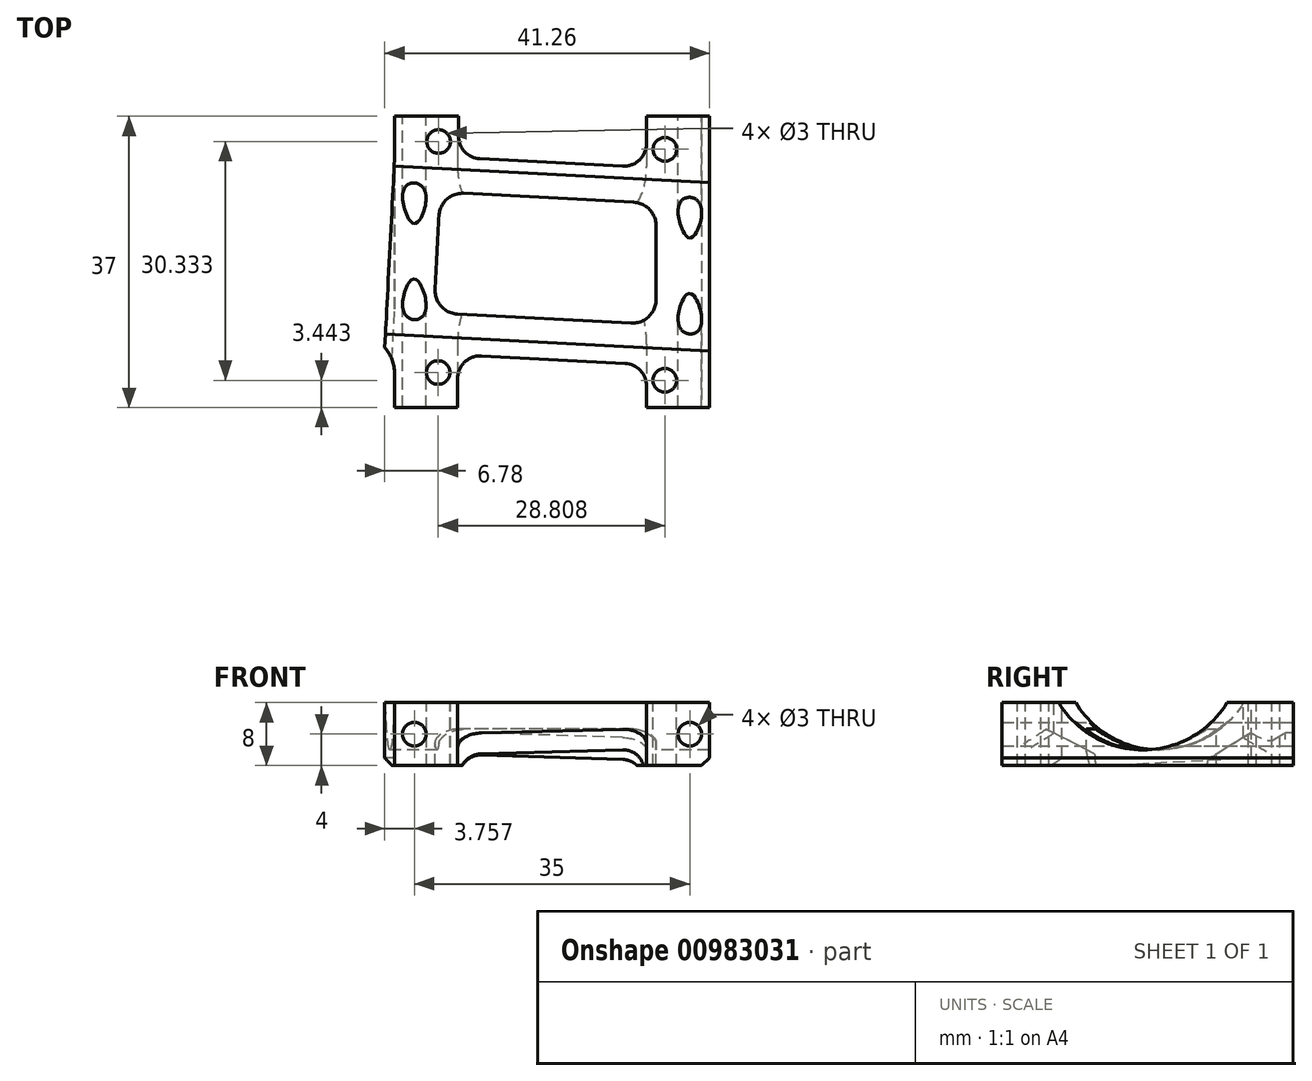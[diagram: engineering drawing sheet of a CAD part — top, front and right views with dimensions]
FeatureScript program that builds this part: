
annotation { "Feature Type Name" : "Feature", "Feature Type Description" : "" }
export const myFeature = defineFeature(function(context is Context, id is Id, definition is map)
    precondition{}
    {
        {
            var Q0;
            Q0=qCreatedBy(makeId("Top.planeOp"),FACE);
            var sketch = newSketch(context, id + "F0", { "sketchPlane" : qUnion([Q0])});
            skLineSegment(sketch, "E0.bottom", {"start": v(-25.77, 33.29) * mm, "end": v(14.23, 33.29) * mm});
            skLineSegment(sketch, "E0.top", {"start": v(-25.77, -1.71) * mm, "end": v(14.23, -1.71) * mm});
            skLineSegment(sketch, "E0.left", {"start": v(-25.77, 33.29) * mm, "end": v(-25.77, -1.71) * mm});
            skLineSegment(sketch, "E0.right", {"start": v(14.23, 33.29) * mm, "end": v(14.23, -1.71) * mm});
            skSolve(sketch);
        }
        {
            var Q0;
            Q0 = qSketchRegion(id + "F0", true);
            extrude(context, id + "F1", {"entities" : qUnion([Q0]), "depth" : 8 * mm, "offsetDistance" : 25 * mm});
        }
        {
            var Q0;
            Q0=makeQuery(id+"F1.opExtrude","CAP_FACE",FACE,{"disambiguationData":[OSD([sQuery(id+"F0.wireOp",EDGE,"E0.bottom"),sQuery(id+"F0.wireOp",EDGE,"E0.top"),sQuery(id+"F0.wireOp",EDGE,"E0.left"),sQuery(id+"F0.wireOp",EDGE,"E0.right")])],"isStart":false});
            var sketch = newSketch(context, id + "F2", { "sketchPlane" : qUnion([Q0])});
            skLineSegment(sketch, "E1", {"start": v(-25.77, 28.93) * mm, "end": v(-27.03, 4.89) * mm});
            skLineSegment(sketch, "E2", {"start": v(-27.03, 4.89) * mm, "end": v(-25.77, 4.82) * mm});
            skLineSegment(sketch, "E3", {"start": v(-25.77, 4.82) * mm, "end": v(-23.4, 26.1) * mm});
            skLineSegment(sketch, "E4", {"start": v(-23.4, 26.1) * mm, "end": v(-25.77, 28.93) * mm});
            skSolve(sketch);
        }
        {
            var Q0;
            Q0 = qSketchRegion(id + "F2", true);
            extrude(context, id + "F3", {"entities" : qUnion([Q0]), "operationType" : NewBodyOperationType.ADD, "oppositeDirection" : true, "depth" : 8 * mm, "offsetDistance" : 25 * mm});
        }
        {
            var Q0;
            Q0=makeQuery(id+"F3.opExtrude","SWEPT_FACE",FACE,{"disambiguationData":[OSD([sQuery(id+"F2.wireOp",EDGE,"E1")])]});
            var sketch = newSketch(context, id + "F4", { "sketchPlane" : qUnion([Q0])});
            skCircle(sketch, "E5", {"center": v(-15.9, 14.5) * mm, "radius": 12.5 * mm});
            skSolve(sketch);
        }
        {
            var Q0;
            Q0 = qSketchRegion(id + "F4", true);
            extrude(context, id + "F5", {"entities" : qUnion([Q0]), "operationType" : NewBodyOperationType.REMOVE, "oppositeDirection" : true, "depth" : 64.1 * mm, "offsetDistance" : 25 * mm});
        }
        {
            var Q0;
            {var subQ1=sQuery(id+"F0.wireOp",EDGE,"E0.left");var subQ2=sQuery(id+"F0.wireOp",EDGE,"E0.right");var subQ3=sQuery(id+"F0.wireOp",EDGE,"E0.bottom");Q0=makeQuery(id+"F5.boolean.opBoolean","SPLIT",FACE,{"disambiguationData":[TD([makeQuery(id+"F1.opExtrude","SWEPT_FACE",FACE,{"disambiguationData":[OSD([subQ3])]})])],"derivedFrom":makeQuery(id+"F3.boolean.opBoolean","MERGE",FACE,{"derivedFrom":[makeQuery(id+"F1.opExtrude","CAP_FACE",FACE,{"disambiguationData":[OSD([subQ3,sQuery(id+"F0.wireOp",EDGE,"E0.top"),subQ1,subQ2])],"isStart":false}),makeQuery(id+"F3.opExtrude","CAP_FACE",FACE,{"disambiguationData":[OSD([sQuery(id+"F2.wireOp",EDGE,"E1"),sQuery(id+"F2.wireOp",EDGE,"E2"),sQuery(id+"F2.wireOp",EDGE,"E3"),sQuery(id+"F2.wireOp",EDGE,"E4")])],"isStart":true})]})});}
            var sketch = newSketch(context, id + "F6", { "sketchPlane" : qUnion([Q0])});
            skLineSegment(sketch, "E6", {"start": v(-14.93, 28.9) * mm, "end": v(3.18, 27.94) * mm});
            skLineSegment(sketch, "E7.0", {"start": v(-14.72, 3.85) * mm, "end": v(3.48, 2.9) * mm});
            skLineSegment(sketch, "E8.0", {"start": v(6.23, 0) * mm, "end": v(6.23, -1.71) * mm});
            skLineSegment(sketch, "E9.0", {"start": v(-17.77, 0.95) * mm, "end": v(-17.77, -1.71) * mm});
            skLineSegment(sketch, "E10.0", {"start": v(6.23, 33.29) * mm, "end": v(6.23, 30.84) * mm});
            skCircle(sketch, "E11", {"center": v(-20.25, 1.73) * mm, "radius": 1.5 * mm});
            skCircle(sketch, "E12", {"center": v(8.56, 30.09) * mm, "radius": 1.5 * mm});
            skCircle(sketch, "E13", {"center": v(-20.2, 31.07) * mm, "radius": 1.5 * mm});
            skLineSegment(sketch, "E14", {"start": v(-17.68, 31.79) * mm, "end": v(-17.68, 33.29) * mm});
            skPoint(sketch, "E15.visualSharp", {"position": v(-17.68, 29.04) * mm});
            skArc(sketch, "E15.filletArc", {"start": v(-17.68, 31.79) * mm, "mid": v(-16.88, 29.8) * mm, "end": v(-14.93, 28.9) * mm});
            skPoint(sketch, "E16.visualSharp", {"position": v(6.23, 27.78) * mm});
            skArc(sketch, "E16.filletArc", {"start": v(3.18, 27.94) * mm, "mid": v(5.32, 28.74) * mm, "end": v(6.23, 30.84) * mm});
            skPoint(sketch, "E17.visualSharp", {"position": v(6.23, 2.75) * mm});
            skArc(sketch, "E17.filletArc", {"start": v(6.23, 0) * mm, "mid": v(5.43, 2) * mm, "end": v(3.48, 2.9) * mm});
            skPoint(sketch, "E18.visualSharp", {"position": v(-17.77, 4) * mm});
            skArc(sketch, "E18.filletArc", {"start": v(-14.72, 3.85) * mm, "mid": v(-16.87, 3.05) * mm, "end": v(-17.77, 0.95) * mm});
            skLineSegment(sketch, "E19", {"start": v(-17.77, -1.71) * mm, "end": v(-10.84, -6.86) * mm});
            skLineSegment(sketch, "E20", {"start": v(-10.84, -6.86) * mm, "end": v(6.23, -1.71) * mm});
            skLineSegment(sketch, "E21", {"start": v(-17.68, 33.29) * mm, "end": v(-3.16, 37.2) * mm});
            skLineSegment(sketch, "E22", {"start": v(-3.16, 37.2) * mm, "end": v(6.23, 33.29) * mm});
            skCircle(sketch, "E23", {"center": v(8.55, 0.73) * mm, "radius": 1.5 * mm});
            skSolve(sketch);
        }
        {
            var Q0;
            Q0 = qSketchRegion(id + "F6", true);
            extrude(context, id + "F7", {"entities" : qUnion([Q0]), "operationType" : NewBodyOperationType.REMOVE, "oppositeDirection" : true, "depth" : 25 * mm, "offsetDistance" : 25 * mm});
        }
        {
            var Q0;
            {var subQ5=sQuery(id+"F0.wireOp",EDGE,"E0.left");var subQ7=sQuery(id+"F0.wireOp",EDGE,"E0.bottom");Q0=makeQuery(id+"F7.boolean.opBoolean","SPLIT",FACE,{"disambiguationData":[TD([makeQuery(id+"F1.opExtrude","SWEPT_FACE",FACE,{"disambiguationData":[OSD([subQ5])]})])],"derivedFrom":makeQuery(id+"F1.opExtrude","SWEPT_FACE",FACE,{"disambiguationData":[OSD([subQ7])]})});}
            var sketch = newSketch(context, id + "F8", { "sketchPlane" : qUnion([Q0])});
            skCircle(sketch, "E24", {"center": v(-11.73, 4) * mm, "radius": 1.5 * mm});
            skCircle(sketch, "E25", {"center": v(23.27, 4) * mm, "radius": 1.5 * mm});
            skSolve(sketch);
        }
        {
            var Q0;
            Q0 = qSketchRegion(id + "F8", true);
            extrude(context, id + "F9", {"entities" : qUnion([Q0]), "operationType" : NewBodyOperationType.REMOVE, "oppositeDirection" : true, "depth" : 46.6 * mm, "offsetDistance" : 25 * mm});
        }
        {
            var Q0;
            Q0=makeQuery(id+"F3.opExtrude","SWEPT_EDGE",EDGE,{"disambiguationData":[OSD([sQuery(id+"F0.wireOp",EDGE,"E0.left"),sQuery(id+"F2.wireOp",EDGE,"E2"),sQuery(id+"F2.wireOp",EDGE,"E3")])]});
            fillet(context, id + "F10", {"entities" : qUnion([Q0]), "radius" : 5 * mm, "tangentPropagation" : true, "allowEdgeOverflow" : false});
        }
        {
            var Q0;
            Q0=makeQuery(id+"F7.boolean.opBoolean","COPY",FACE,{"derivedFrom":makeQuery(id+"F7.opExtrude","SWEPT_FACE",FACE,{"disambiguationData":[OSD([sQuery(id+"F6.wireOp",EDGE,"E8.0")])]})});
            var sketch = newSketch(context, id + "F11", { "sketchPlane" : qUnion([Q0])});
            skLineSegment(sketch, "E26", {"start": v(-37.97, 9.77) * mm, "end": v(-21.04, -0.7) * mm});
            skLineSegment(sketch, "E27", {"start": v(-13.35, -0.7) * mm, "end": v(0, 6.1) * mm});
            skLineSegment(sketch, "E28", {"start": v(-37.97, 9.77) * mm, "end": v(-37.97, -11.82) * mm});
            skLineSegment(sketch, "E29", {"start": v(-37.97, -11.82) * mm, "end": v(-21.04, -0.7) * mm});
            skLineSegment(sketch, "E30", {"start": v(-13.35, -0.7) * mm, "end": v(-2.57, -3.45) * mm});
            skLineSegment(sketch, "E31", {"start": v(0, 6.1) * mm, "end": v(4.72, 8.5) * mm});
            skLineSegment(sketch, "E32", {"start": v(4.72, 8.5) * mm, "end": v(6.07, -10.58) * mm});
            skLineSegment(sketch, "E33", {"start": v(6.07, -10.58) * mm, "end": v(-2.57, -3.45) * mm});
            skSolve(sketch);
        }
        {
            var Q0;
            Q0 = qSketchRegion(id + "F11", true);
            var Q1;
            Q1=makeQuery(id+"F7.boolean.opBoolean","COPY",FACE,{"derivedFrom":makeQuery(id+"F7.opExtrude","SWEPT_FACE",FACE,{"disambiguationData":[OSD([sQuery(id+"F6.wireOp",EDGE,"E9.0")])]})});
            extrude(context, id + "F12", {"entities" : qUnion([Q0]), "operationType" : NewBodyOperationType.REMOVE, "endBound" : BoundingType.UP_TO_SURFACE, "depth" : 25 * mm, "endBoundEntityFace" : qUnion([Q1]), "offsetDistance" : 25 * mm});
        }
        {
            var Q0;
            Q0=makeQuery(id+"F12.boolean.opBoolean","COPY",EDGE,{"derivedFrom":makeQuery(id+"F12.opExtrude","CAP_EDGE",EDGE,{"disambiguationData":[OSD([sQuery(id+"F11.wireOp",EDGE,"E26")])],"isStart":true})});
            var Q1;
            Q1=makeQuery(id+"F12.boolean.opBoolean","COPY",EDGE,{"derivedFrom":makeQuery(id+"F12.opExtrude","CAP_EDGE",EDGE,{"disambiguationData":[OSD([sQuery(id+"F11.wireOp",EDGE,"E27")])],"isStart":false})});
            var Q2;
            Q2=makeQuery(id+"F12.boolean.opBoolean","COPY",EDGE,{"derivedFrom":makeQuery(id+"F12.opExtrude","CAP_EDGE",EDGE,{"disambiguationData":[OSD([sQuery(id+"F11.wireOp",EDGE,"E26")])],"isStart":false})});
            var Q3;
            Q3=makeQuery(id+"F12.boolean.opBoolean","COPY",EDGE,{"derivedFrom":makeQuery(id+"F12.opExtrude","CAP_EDGE",EDGE,{"disambiguationData":[OSD([sQuery(id+"F11.wireOp",EDGE,"E27")])],"isStart":true})});
            fillet(context, id + "F13", {"entities" : qUnion([Q0, Q1, Q2, Q3]), "radius" : 3 * mm, "tangentPropagation" : true, "allowEdgeOverflow" : false});
        }
        {
            var Q0;
            Q0=makeQuery(id+"F1.opExtrude","CAP_EDGE",EDGE,{"disambiguationData":[OSD([sQuery(id+"F0.wireOp",EDGE,"E0.right")])],"isStart":true});
            var Q1;
            Q1=makeQuery(id+"F3.opExtrude","CAP_EDGE",EDGE,{"disambiguationData":[OSD([sQuery(id+"F2.wireOp",EDGE,"E1")])],"isStart":false});
            chamfer(context, id + "F14", {"entities" : qUnion([Q0, Q1]), "width" : 1 * mm, "tangentPropagation" : true});
        }
        {
            var Q0;
            {var subQ4=sQuery(id+"F0.wireOp",EDGE,"E0.right");var subQ6=sQuery(id+"F0.wireOp",EDGE,"E0.top");Q0=makeQuery(id+"F7.boolean.opBoolean","SPLIT",FACE,{"disambiguationData":[TD([makeQuery(id+"F1.opExtrude","SWEPT_FACE",FACE,{"disambiguationData":[OSD([subQ4])]})])],"derivedFrom":makeQuery(id+"F1.opExtrude","SWEPT_FACE",FACE,{"disambiguationData":[OSD([subQ6])]})});}
            var Q1;
            {var subQ5=sQuery(id+"F0.wireOp",EDGE,"E0.left");var subQ6=sQuery(id+"F0.wireOp",EDGE,"E0.top");Q1=makeQuery(id+"F7.boolean.opBoolean","SPLIT",FACE,{"disambiguationData":[TD([makeQuery(id+"F1.opExtrude","SWEPT_FACE",FACE,{"disambiguationData":[OSD([subQ5])]})])],"derivedFrom":makeQuery(id+"F1.opExtrude","SWEPT_FACE",FACE,{"disambiguationData":[OSD([subQ6])]})});}
            extrude(context, id + "F15", {"entities" : qUnion([Q0, Q1]), "operationType" : NewBodyOperationType.ADD, "depth" : 1 * mm, "offsetDistance" : 25 * mm});
        }
        {
            var Q0;
            {var subQ4=sQuery(id+"F0.wireOp",EDGE,"E0.right");var subQ7=sQuery(id+"F0.wireOp",EDGE,"E0.bottom");Q0=makeQuery(id+"F7.boolean.opBoolean","SPLIT",FACE,{"disambiguationData":[TD([makeQuery(id+"F1.opExtrude","SWEPT_FACE",FACE,{"disambiguationData":[OSD([subQ4])]})])],"derivedFrom":makeQuery(id+"F1.opExtrude","SWEPT_FACE",FACE,{"disambiguationData":[OSD([subQ7])]})});}
            var Q1;
            {var subQ5=sQuery(id+"F0.wireOp",EDGE,"E0.left");var subQ7=sQuery(id+"F0.wireOp",EDGE,"E0.bottom");Q1=makeQuery(id+"F7.boolean.opBoolean","SPLIT",FACE,{"disambiguationData":[TD([makeQuery(id+"F1.opExtrude","SWEPT_FACE",FACE,{"disambiguationData":[OSD([subQ5])]})])],"derivedFrom":makeQuery(id+"F1.opExtrude","SWEPT_FACE",FACE,{"disambiguationData":[OSD([subQ7])]})});}
            extrude(context, id + "F16", {"entities" : qUnion([Q0, Q1]), "operationType" : NewBodyOperationType.ADD, "depth" : 1 * mm, "offsetDistance" : 25 * mm});
        }
        {
            var Q0;
            {var subQ0=sQuery(id+"F2.wireOp",EDGE,"E1");var subQ1=makeQuery(id+"F3.opExtrude","CAP_FACE",FACE,{"disambiguationData":[OSD([subQ0,sQuery(id+"F2.wireOp",EDGE,"E2"),sQuery(id+"F2.wireOp",EDGE,"E3"),sQuery(id+"F2.wireOp",EDGE,"E4")])],"isStart":true});var subQ2=sQuery(id+"F0.wireOp",EDGE,"E0.right");var subQ3=sQuery(id+"F0.wireOp",EDGE,"E0.left");var subQ4=sQuery(id+"F0.wireOp",EDGE,"E0.bottom");var subQ5=makeQuery(id+"F1.opExtrude","CAP_FACE",FACE,{"disambiguationData":[OSD([subQ4,sQuery(id+"F0.wireOp",EDGE,"E0.top"),subQ3,subQ2])],"isStart":false});var subQ6=makeQuery(id+"F1.opExtrude","SWEPT_FACE",FACE,{"disambiguationData":[OSD([subQ2])]});var subQ7=makeQuery(id+"F1.opExtrude","SWEPT_FACE",FACE,{"disambiguationData":[OSD([subQ4])]});var subQ8=makeQuery(id+"F1.opExtrude","CAP_EDGE",EDGE,{"disambiguationData":[OSD([subQ4])],"isStart":false});var subQ9=makeQuery(id+"F1.opExtrude","SWEPT_FACE",FACE,{"disambiguationData":[OSD([subQ3])]});Q0=makeQuery(id+"F16.boolean.opBoolean","MERGE",FACE,{"derivedFrom":[makeQuery(id+"F5.boolean.opBoolean","SPLIT",FACE,{"disambiguationData":[TD([subQ7])],"derivedFrom":makeQuery(id+"F3.boolean.opBoolean","MERGE",FACE,{"derivedFrom":[subQ5,subQ1]})}),makeQuery(id+"F16.opExtrude","SWEPT_FACE",FACE,{"disambiguationData":[OSD([subQ4]),TDD([makeQuery(id+"F7.boolean.opBoolean","SPLIT",EDGE,{"disambiguationData":[TD([subQ9])],"derivedFrom":subQ8})])]}),makeQuery(id+"F16.opExtrude","SWEPT_FACE",FACE,{"disambiguationData":[OSD([subQ4]),TDD([makeQuery(id+"F7.boolean.opBoolean","SPLIT",EDGE,{"disambiguationData":[TD([subQ6])],"derivedFrom":subQ8})])]})]});}
            var sketch = newSketch(context, id + "F17", { "sketchPlane" : qUnion([Q0])});
            skLineSegment(sketch, "E34.0", {"start": v(4.58, 23.36) * mm, "end": v(-17, 24.5) * mm});
            skLineSegment(sketch, "E34.2", {"start": v(-17.8, 9.16) * mm, "end": v(4.27, 8) * mm});
            skLineSegment(sketch, "E35.3", {"start": v(-20.15, 21.65) * mm, "end": v(-20.64, 12.31) * mm});
            skLineSegment(sketch, "E36", {"start": v(14.23, 25.86) * mm, "end": v(14.23, 2.64) * mm});
            skLineSegment(sketch, "E37.0", {"start": v(7.43, 20.37) * mm, "end": v(7.43, 11) * mm});
            skPoint(sketch, "E38.visualSharp", {"position": v(-19.99, 24.65) * mm});
            skArc(sketch, "E38.filletArc", {"start": v(-17, 24.5) * mm, "mid": v(-19.16, 23.73) * mm, "end": v(-20.15, 21.65) * mm});
            skPoint(sketch, "E39.visualSharp", {"position": v(-20.8, 9.32) * mm});
            skArc(sketch, "E39.filletArc", {"start": v(-20.64, 12.31) * mm, "mid": v(-19.87, 10.15) * mm, "end": v(-17.8, 9.16) * mm});
            skPoint(sketch, "E40.visualSharp", {"position": v(7.43, 7.84) * mm});
            skArc(sketch, "E40.filletArc", {"start": v(4.27, 8) * mm, "mid": v(6.5, 8.82) * mm, "end": v(7.43, 11) * mm});
            skPoint(sketch, "E41.visualSharp", {"position": v(7.43, 23.21) * mm});
            skArc(sketch, "E41.filletArc", {"start": v(7.43, 20.37) * mm, "mid": v(6.6, 22.43) * mm, "end": v(4.58, 23.36) * mm});
            skSolve(sketch);
        }
        {
            var Q0;
            Q0 = qSketchRegion(id + "F17", true);
            extrude(context, id + "F18", {"entities" : qUnion([Q0]), "operationType" : NewBodyOperationType.REMOVE, "oppositeDirection" : true, "depth" : 25 * mm, "offsetDistance" : 25 * mm});
        }
    });
